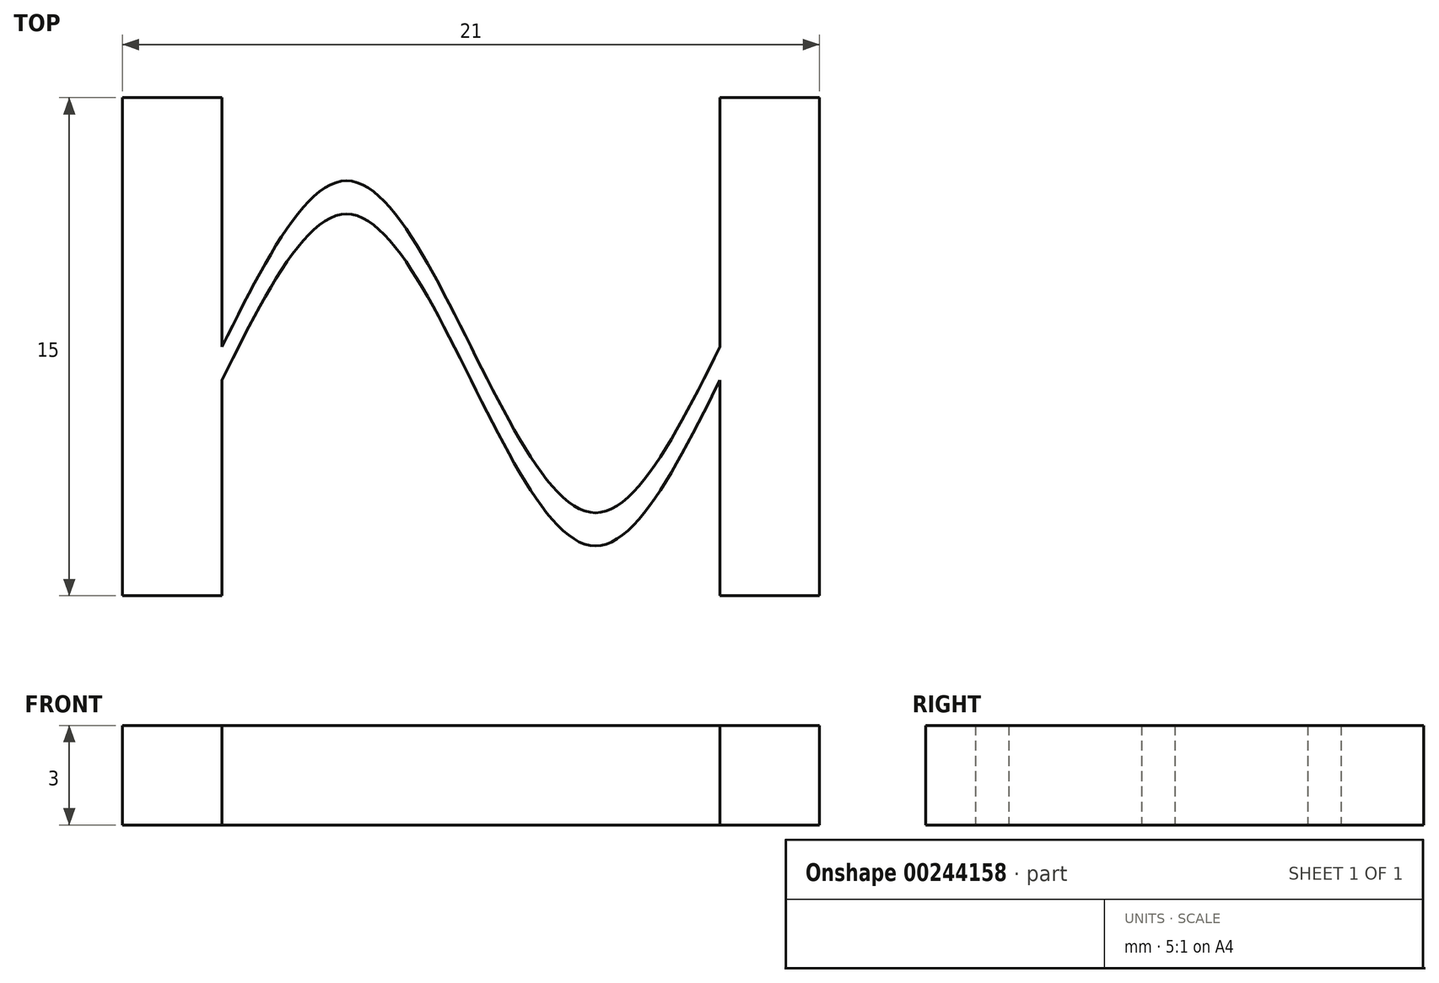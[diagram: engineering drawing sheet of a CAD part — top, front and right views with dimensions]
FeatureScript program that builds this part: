
annotation { "Feature Type Name" : "Feature", "Feature Type Description" : "" }
export const myFeature = defineFeature(function(context is Context, id is Id, definition is map)
    precondition{}
    {
        {
            var Q0;
            Q0=qCreatedBy(makeId("Top.planeOp"),FACE);
            var sketch = newSketch(context, id + "F0", { "sketchPlane" : qUnion([Q0])});
            skLineSegment(sketch, "E0", {"start": v(0, 0) * mm, "end": v(0, 15) * mm});
            skLineSegment(sketch, "E1", {"start": v(0, 15) * mm, "end": v(3, 15) * mm});
            skLineSegment(sketch, "E2", {"start": v(0, 0) * mm, "end": v(3, 0) * mm});
            skLineSegment(sketch, "E3", {"start": v(3, 7.5) * mm, "end": v(18, 7.5) * mm, "construction": true});
            skLineSegment(sketch, "E4", {"start": v(3, 7.5) * mm, "end": v(10.5, 7.5) * mm, "construction": true});
            skLineSegment(sketch, "E5", {"start": v(10.5, 7.5) * mm, "end": v(18, 7.5) * mm, "construction": true});
            skLineSegment(sketch, "E6", {"start": v(6.75, 7.5) * mm, "end": v(6.75, 12.5) * mm, "construction": true});
            skLineSegment(sketch, "E7", {"start": v(14.25, 7.5) * mm, "end": v(14.25, 2.5) * mm, "construction": true});
            skLineSegment(sketch, "E8", {"start": v(18, 0) * mm, "end": v(21, 0) * mm});
            skLineSegment(sketch, "E9", {"start": v(21, 0) * mm, "end": v(21, 15) * mm});
            skLineSegment(sketch, "E10", {"start": v(21, 15) * mm, "end": v(18, 15) * mm});
            skFitSpline(sketch, "E11", {"points": [v(3, 7.5) * mm, v(6.75, 12.5) * mm, v(10.5, 7.5) * mm, v(14.25, 2.5) * mm, v(18, 7.5) * mm], "startDerivative": vector(15, 30) * mm, "endDerivative": vector(15, 30) * mm});
            skLineSegment(sketch, "E12", {"start": v(3, 7.5) * mm, "end": v(3, 6.5) * mm});
            skLineSegment(sketch, "E13", {"start": v(6.75, 12.5) * mm, "end": v(6.75, 11.5) * mm});
            skLineSegment(sketch, "E14", {"start": v(10.5, 7.5) * mm, "end": v(10.5, 6.5) * mm});
            skLineSegment(sketch, "E15", {"start": v(14.25, 2.5) * mm, "end": v(14.25, 1.5) * mm});
            skLineSegment(sketch, "E16", {"start": v(18, 7.5) * mm, "end": v(18, 6.5) * mm});
            skFitSpline(sketch, "E17", {"points": [v(3, 6.5) * mm, v(6.75, 11.5) * mm, v(10.5, 6.5) * mm, v(14.25, 1.5) * mm, v(18, 6.5) * mm], "startDerivative": vector(15, 30) * mm, "endDerivative": vector(15, 30) * mm});
            skLineSegment(sketch, "E18", {"start": v(18, 15) * mm, "end": v(18, 7.5) * mm});
            skLineSegment(sketch, "E19", {"start": v(3, 15) * mm, "end": v(3, 7.5) * mm});
            skLineSegment(sketch, "E20", {"start": v(3, 6.5) * mm, "end": v(3, 0) * mm});
            skLineSegment(sketch, "E21", {"start": v(18, 6.5) * mm, "end": v(18, 0) * mm});
            skSolve(sketch);
        }
        {
            var Q0;
            Q0 = qSketchRegion(id + "F0", true);
            extrude(context, id + "F1", {"entities" : qUnion([Q0]), "depth" : 3 * mm});
        }
    });
